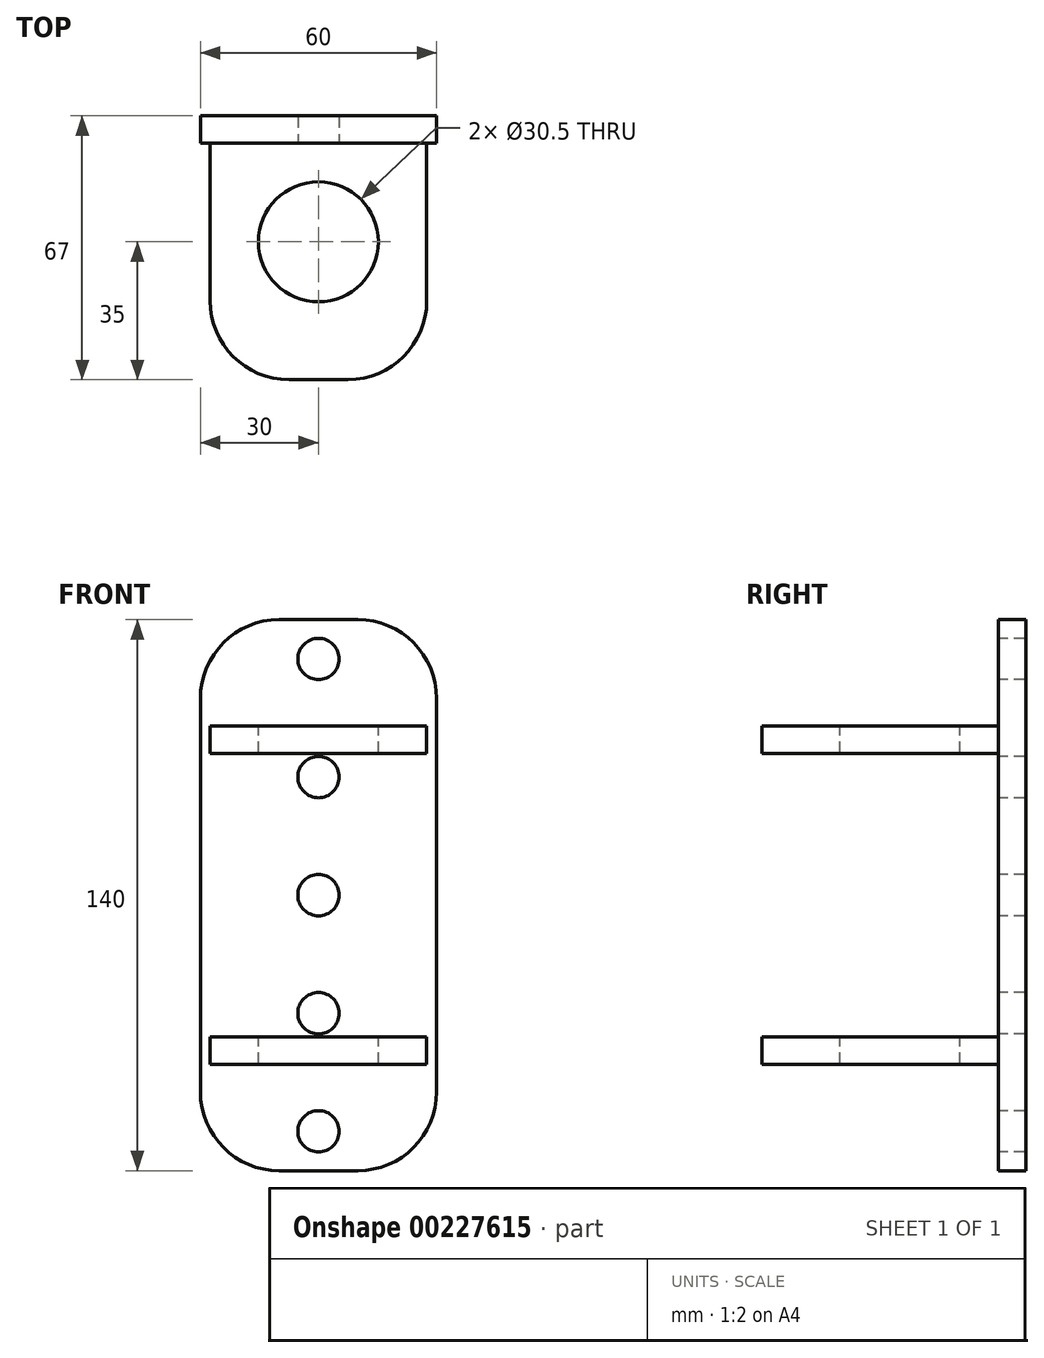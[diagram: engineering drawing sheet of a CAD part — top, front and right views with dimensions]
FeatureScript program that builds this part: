
annotation { "Feature Type Name" : "Feature", "Feature Type Description" : "" }
export const myFeature = defineFeature(function(context is Context, id is Id, definition is map)
    precondition{}
    {
        {
            var Q0;
            Q0=qCreatedBy(makeId("Front.planeOp"),FACE);
            var sketch = newSketch(context, id + "F0", { "sketchPlane" : qUnion([Q0])});
            skLineSegment(sketch, "E0.bottom", {"start": v(30, 70) * mm, "end": v(-30, 70) * mm});
            skLineSegment(sketch, "E0.top", {"start": v(30, -70) * mm, "end": v(-30, -70) * mm});
            skLineSegment(sketch, "E0.left", {"start": v(30, 70) * mm, "end": v(30, -70) * mm});
            skLineSegment(sketch, "E0.right", {"start": v(-30, 70) * mm, "end": v(-30, -70) * mm});
            skPoint(sketch, "E0.middle", {"position": v(0, 0) * mm});
            skCircle(sketch, "E1", {"center": v(0, 0) * mm, "radius": 5.25 * mm});
            skCircle(sketch, "E2", {"center": v(0, 30) * mm, "radius": 5.25 * mm});
            skCircle(sketch, "E3", {"center": v(0, -30) * mm, "radius": 5.25 * mm});
            skCircle(sketch, "E4", {"center": v(0, 60) * mm, "radius": 5.25 * mm});
            skCircle(sketch, "E5", {"center": v(0, -60) * mm, "radius": 5.25 * mm});
            skSolve(sketch);
        }
        {
            var Q0;
            Q0 = qSketchRegion(id + "F0", true);
            extrude(context, id + "F1", {"entities" : qUnion([Q0]), "oppositeDirection" : true, "depth" : 7 * mm});
        }
        {
            var Q0;
            Q0=qCreatedBy(makeId("Right.planeOp"),FACE);
            var sketch = newSketch(context, id + "F2", { "sketchPlane" : qUnion([Q0])});
            skLineSegment(sketch, "E6", {"start": v(0, 0) * mm, "end": v(-34.64, 0) * mm, "construction": true});
            skLineSegment(sketch, "E7", {"start": v(0, 36) * mm, "end": v(0, 43) * mm});
            skLineSegment(sketch, "E8", {"start": v(0, 43) * mm, "end": v(-60, 43) * mm});
            skLineSegment(sketch, "E9", {"start": v(-60, 43) * mm, "end": v(-60, 36) * mm});
            skLineSegment(sketch, "E10", {"start": v(-60, 36) * mm, "end": v(0, 36) * mm});
            skLineSegment(sketch, "E11", {"start": v(0, -36) * mm, "end": v(-60, -36) * mm});
            skLineSegment(sketch, "E12", {"start": v(-60, -36) * mm, "end": v(-60, -43) * mm});
            skLineSegment(sketch, "E13", {"start": v(-60, -43) * mm, "end": v(0, -43) * mm});
            skLineSegment(sketch, "E14", {"start": v(0, -43) * mm, "end": v(0, -36) * mm});
            skSolve(sketch);
        }
        {
            var Q0;
            Q0 = qSketchRegion(id + "F2", true);
            extrude(context, id + "F3", {"entities" : qUnion([Q0]), "operationType" : NewBodyOperationType.ADD, "endBound" : BoundingType.SYMMETRIC, "depth" : 55 * mm});
        }
        {
            var Q0;
            Q0=makeQuery(id+"F3.opExtrude","SWEPT_FACE",FACE,{"disambiguationData":[OSD([sQuery(id+"F2.wireOp",EDGE,"E8")])]});
            var sketch = newSketch(context, id + "F4", { "sketchPlane" : qUnion([Q0])});
            skLineSegment(sketch, "E15", {"start": v(0, 0) * mm, "end": v(0, -60) * mm, "construction": true});
            skCircle(sketch, "E16", {"center": v(0, -25) * mm, "radius": 15.25 * mm});
            skSolve(sketch);
        }
        {
            var Q0;
            Q0 = qSketchRegion(id + "F4", true);
            extrude(context, id + "F5", {"entities" : qUnion([Q0]), "operationType" : NewBodyOperationType.REMOVE, "endBound" : BoundingType.THROUGH_ALL, "oppositeDirection" : true, "depth" : 25 * mm});
        }
        {
            var Q0;
            Q0=makeQuery(id+"F1.opExtrude","SWEPT_EDGE",EDGE,{"disambiguationData":[OSD([sQuery(id+"F0.wireOp",EDGE,"E0.bottom"),sQuery(id+"F0.wireOp",EDGE,"E0.right")])]});
            var Q1;
            Q1=makeQuery(id+"F1.opExtrude","SWEPT_EDGE",EDGE,{"disambiguationData":[OSD([sQuery(id+"F0.wireOp",EDGE,"E0.bottom"),sQuery(id+"F0.wireOp",EDGE,"E0.left")])]});
            var Q2;
            Q2=makeQuery(id+"F3.opExtrude","CAP_EDGE",EDGE,{"disambiguationData":[OSD([sQuery(id+"F2.wireOp",EDGE,"E9")])],"isStart":true});
            var Q3;
            Q3=makeQuery(id+"F3.opExtrude","CAP_EDGE",EDGE,{"disambiguationData":[OSD([sQuery(id+"F2.wireOp",EDGE,"E9")])],"isStart":false});
            var Q4;
            Q4=makeQuery(id+"F3.opExtrude","CAP_EDGE",EDGE,{"disambiguationData":[OSD([sQuery(id+"F2.wireOp",EDGE,"E12")])],"isStart":true});
            var Q5;
            Q5=makeQuery(id+"F3.opExtrude","CAP_EDGE",EDGE,{"disambiguationData":[OSD([sQuery(id+"F2.wireOp",EDGE,"E12")])],"isStart":false});
            var Q6;
            Q6=makeQuery(id+"F1.opExtrude","SWEPT_EDGE",EDGE,{"disambiguationData":[OSD([sQuery(id+"F0.wireOp",EDGE,"E0.top"),sQuery(id+"F0.wireOp",EDGE,"E0.right")])]});
            var Q7;
            Q7=makeQuery(id+"F1.opExtrude","SWEPT_EDGE",EDGE,{"disambiguationData":[OSD([sQuery(id+"F0.wireOp",EDGE,"E0.top"),sQuery(id+"F0.wireOp",EDGE,"E0.left")])]});
            fillet(context, id + "F6", {"entities" : qUnion([Q0, Q1, Q2, Q3, Q4, Q5, Q6, Q7]), "radius" : 20 * mm, "tangentPropagation" : true, "allowEdgeOverflow" : false});
        }
    });
